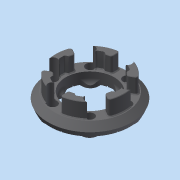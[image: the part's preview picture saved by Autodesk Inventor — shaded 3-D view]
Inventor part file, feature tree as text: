
AUTODESK INVENTOR PART (.ipt)
format: ipt  version: 2014 SP1 (Build 180222100, 222)  size: 949,760 bytes
history: native  units: in
note: dims shown in document units (in); Inventor stores cm internally (conversion verified against a paired STEP export)
features: extrude x7, chamfer x6, projected_geometry x5, sketch x4, fillet x3, other x1, pattern_circular x1
ambient origin geometry x8: Origin, YZ Plane, XZ Plane, XY Plane, X Axis, Y Axis, Z Axis, Center Point
bodies: Solid1 (feature_tree)
feature tree (27):
  other  "wheelinsertsketch.ipt"
  extrude  "Extrusion1"  Depth=0.3937in TaperAngle=0.0deg
  extrude  "Extrusion2"  Depth=0.25in TaperAngle=0.0deg
  chamfer  "Chamfer1"  Distance=0.25in Angle=45.0deg
  chamfer  "Chamfer6"  Distance=0.1625in Angle=45.0deg
  extrude  "Extrusion6"  Depth=0.375in
  extrude  "Extrusion9"  Depth=2.0in
  sketch  "Sketch6"  dims[d3=2.15in d4=0.25in d5=0.0in d6=0.25in d7=0.125in d8=45.0deg d42=0.1625in d43=0.125in d44=45.0deg]
  extrude  "Extrusion7"  Depth=2.0in
  chamfer  "Chamfer9"  Distance=0.375in
  fillet  "Fillet6"  Radius=0.375in
  fillet  "Fillet7"  Radius=0.01in
  extrude  "Extrusion10"  Depth=2.0in
  chamfer  "Chamfer10"  Distance=0.01in
  extrude  "Extrusion11"  Depth=2.0in TaperAngle=360.0deg
  chamfer  "Chamfer11"  Distance=0.02in
  pattern_circular  "Circular Pattern1"  Angle=45.0deg  [1 undecoded]
  chamfer  "Chamfer12"  Distance=0.15in
  fillet  "Fillet8"  Radius=0.145in
  sketch  "Sketch5"  dims[d0=0.3937in d1=0.35in d2=0.0in]
  projected_geometry  "Projected Loop3"
  projected_geometry  "Projected Loop4"
  projected_geometry  "Projected Loop5"
  sketch  "Sketch8"  dims[d45=1.0in d46=0.0in d47=0.375in]
  projected_geometry  "Projected Loop12"
  sketch  "Sketch9"  dims[d48=0.375in d49=0.375in d50=0.375in d51=0.375in d52=0.375in d53=0.01in d54=0.0in d67=0.01in d68=0.01in d69=2.3622in d71=360.0deg d73=0.02in d74=0.0in d78=0.047in d79=0.125in d80=45.0deg d81=0.15in d82=0.145in d83=0.05in d84=0.0in d85=0.05in d86=0.125in d87=45.0deg d88=0.0197in d89=0.0197in d90=0.0in d91=0.0197in d92=0.125in d93=45.0deg d94=0.0098in d95=0.125in d96=45.0deg d97=2.0in d98=2.3622in d99=360.0deg]
  projected_geometry  "Projected Loop13"
note: 1 required parameter value undecoded (feature->parameter linkage not recoverable at this tier; creation-order binding heuristic only, values carry confidence <= 0.55)
